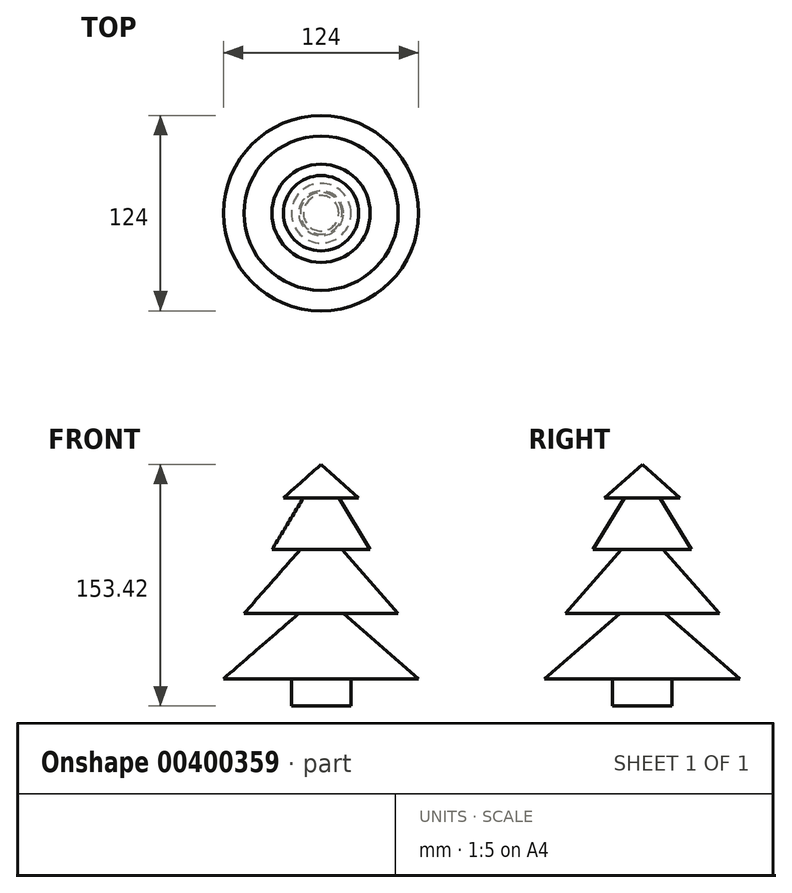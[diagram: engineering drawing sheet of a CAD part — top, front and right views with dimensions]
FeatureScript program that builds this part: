
annotation { "Feature Type Name" : "Feature", "Feature Type Description" : "" }
export const myFeature = defineFeature(function(context is Context, id is Id, definition is map)
    precondition{}
    {
        {
            var Q0;
            Q0=qCreatedBy(makeId("Front.planeOp"),FACE);
            var sketch = newSketch(context, id + "F0", { "sketchPlane" : qUnion([Q0])});
            skLineSegment(sketch, "E0", {"start": v(0, 77.15) * mm, "end": v(23.9, 55.82) * mm});
            skLineSegment(sketch, "E1", {"start": v(23.9, 55.82) * mm, "end": v(11.25, 55.82) * mm});
            skLineSegment(sketch, "E2", {"start": v(11.25, 55.82) * mm, "end": v(31.2, 23.05) * mm});
            skLineSegment(sketch, "E3", {"start": v(31.2, 23.05) * mm, "end": v(13.23, 23.05) * mm});
            skLineSegment(sketch, "E4", {"start": v(13.23, 23.05) * mm, "end": v(48.97, -17.62) * mm});
            skLineSegment(sketch, "E5", {"start": v(48.97, -17.62) * mm, "end": v(14.22, -17.62) * mm});
            skLineSegment(sketch, "E6", {"start": v(14.22, -17.62) * mm, "end": v(62, -59.09) * mm});
            skLineSegment(sketch, "E7", {"start": v(62, -59.09) * mm, "end": v(18.95, -59.09) * mm});
            skLineSegment(sketch, "E8", {"start": v(18.95, -59.09) * mm, "end": v(18.95, -76.27) * mm});
            skLineSegment(sketch, "E9", {"start": v(18.95, -76.27) * mm, "end": v(0, -76.27) * mm});
            skLineSegment(sketch, "E10", {"start": v(0, -76.27) * mm, "end": v(0, 77.15) * mm});
            skSolve(sketch);
        }
        {
            var Q0;
            Q0=makeQuery(id+"F0.imprint","IMPRINT",FACE,{"disambiguationData":[TD([[makeQuery(id+"F0.imprint","IMPRINT",EDGE,{"derivedFrom":sQuery(id+"F0.wireOp",EDGE,"E0")}),-1.0]])]});
            var Q1;
            Q1=sQuery(id+"F0.wireOp",EDGE,"E10");
            revolve(context, id + "F1", {"entities" : qUnion([Q0]), "axis" : qUnion([Q1]), "revolveType" : RevolveType.FULL});
        }
    });
